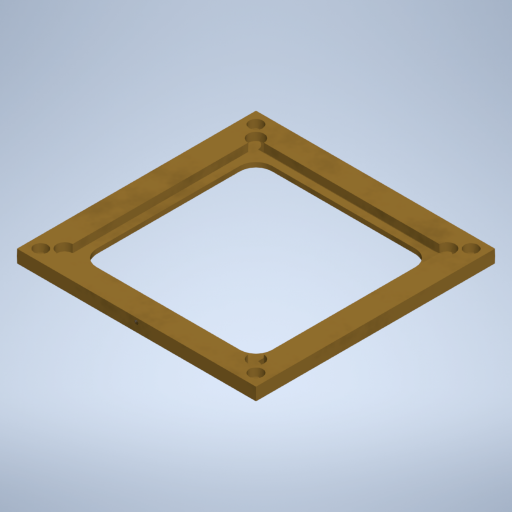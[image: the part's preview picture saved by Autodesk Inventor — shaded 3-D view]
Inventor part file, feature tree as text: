
AUTODESK INVENTOR PART (.ipt)
format: ipt  version: 2023 (Build 270158000, 158)  size: 356,352 bytes
history: native  units: mm
features: sketch x6, extrude x4, hole x2, other x1
ambient origin geometry x8: Origin, YZ Plane, XZ Plane, XY Plane, X Axis, Y Axis, Z Axis, Center Point
bodies: Body1 (feature_tree)
feature tree (13):
  other  "Sólido1"
  extrude  "Extrusão1"  Depth=150.0mm
  extrude  "Extrusão2"  Depth=120.0mm
  extrude  "Extrusão3"  TaperAngle=0.0deg  [1 undecoded]
  extrude  "Extrusão4"  Depth=5.0mm TaperAngle=0.0deg
  hole  "Furo1"  [1 undecoded]
  hole  "Furo2"  [1 undecoded]
  sketch  "Esboço1"  dims[d0=150.0mm d1=150.0mm]
  sketch  "Esboço2"  dims[d2=8.0mm d3=0.0mm d4=120.0mm]
  sketch  "Esboço3"  dims[d5=120.0mm d6=0.0mm]
  sketch  "Esboço4"  dims[d7=0.0mm d8=5.0mm d9=0.0mm]
  sketch  "Esboço5"  dims[d10=110.0mm d11=0.0mm]
  sketch  "Esboço6"  dims[d12=0.0mm d13=3.0mm d14=0.0mm d15=10.0mm d16=0.0mm d17=0.0mm d18=0.0mm d19=0.0mm d20=0.0mm d21=0.0mm d22=0.0mm d23=0.0mm d24=5.0mm d25=0.0mm d26=5.0mm d27=2.5mm d28=0.0mm d29=2.459mm d30=100.0mm d31=4.0mm d32=2.0mm d33=90.0deg d34=8.8mm d35=20.594885mm d36=7.5mm d37=15.0mm d38=7.5mm d39=7.5mm d40=7.5mm d41=7.5mm d42=7.5mm d43=7.5mm d44=7.5mm d45=5.0mm d46=10.0mm d47=8.5mm d48=5.0mm d49=90.0deg d50=8.0mm d51=20.594885mm d52=10.0mm]
note: 3 required parameter values undecoded (feature->parameter linkage not recoverable at this tier; creation-order binding heuristic only, values carry confidence <= 0.55)
